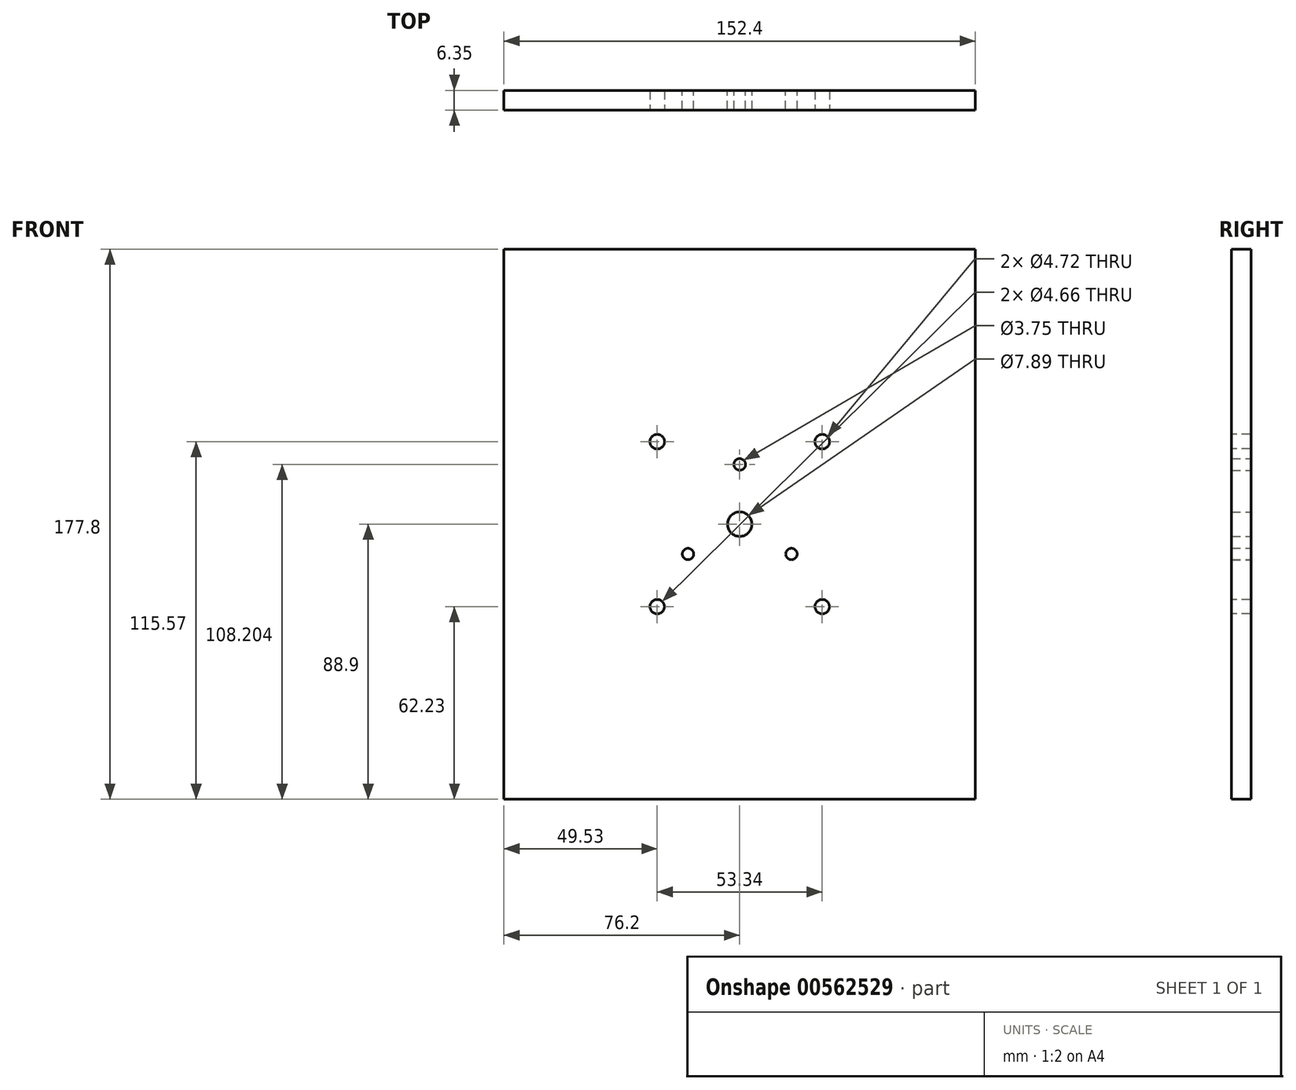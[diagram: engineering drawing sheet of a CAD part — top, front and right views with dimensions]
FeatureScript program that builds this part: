
annotation { "Feature Type Name" : "Feature", "Feature Type Description" : "" }
export const myFeature = defineFeature(function(context is Context, id is Id, definition is map)
    precondition{}
    {
        {
            var Q0;
            Q0=qCreatedBy(makeId("Front.planeOp"),FACE);
            var sketch = newSketch(context, id + "F0", { "sketchPlane" : qUnion([Q0])});
            skLineSegment(sketch, "E0.bottom", {"start": v(76.2, 88.9) * mm, "end": v(-76.2, 88.9) * mm});
            skLineSegment(sketch, "E0.top", {"start": v(76.2, -88.9) * mm, "end": v(-76.2, -88.9) * mm});
            skLineSegment(sketch, "E0.left", {"start": v(76.2, 88.9) * mm, "end": v(76.2, -88.9) * mm});
            skLineSegment(sketch, "E0.right", {"start": v(-76.2, 88.9) * mm, "end": v(-76.2, -88.9) * mm});
            skPoint(sketch, "E0.middle", {"position": v(0, 0) * mm});
            skLineSegment(sketch, "E1", {"start": v(0, 0) * mm, "end": v(0, 83.85) * mm, "construction": true});
            skLineSegment(sketch, "E2", {"start": v(0, 0) * mm, "end": v(67.53, -38.99) * mm, "construction": true});
            skLineSegment(sketch, "E3", {"start": v(0, 0) * mm, "end": v(-59.92, -34.6) * mm, "construction": true});
            skLineSegment(sketch, "E4", {"start": v(-11.78, 19.3) * mm, "end": v(15.02, 19.3) * mm, "construction": true});
            skLineSegment(sketch, "E5", {"start": v(20.55, -3.01) * mm, "end": v(11.36, -18.94) * mm, "construction": true});
            skLineSegment(sketch, "E6", {"start": v(-21.54, -0.84) * mm, "end": v(-10.74, -20.58) * mm, "construction": true});
            skCircle(sketch, "E7", {"center": v(-16.72, -9.65) * mm, "radius": 1.84 * mm});
            skCircle(sketch, "E8", {"center": v(16.72, -9.65) * mm, "radius": 1.85 * mm});
            skCircle(sketch, "E9", {"center": v(0, 19.3) * mm, "radius": 1.87 * mm});
            skCircle(sketch, "E10", {"center": v(0, 0) * mm, "radius": 3.94 * mm});
            skSolve(sketch);
        }
        {
            var Q0;
            Q0=makeQuery(id+"F0.imprint","IMPRINT",FACE,{"disambiguationData":[TD([[makeQuery(id+"F0.imprint","IMPRINT",EDGE,{"derivedFrom":sQuery(id+"F0.wireOp",EDGE,"E0.bottom")}),1.0]])]});
            extrude(context, id + "F1", {"entities" : qUnion([Q0]), "depth" : 6.35 * mm, "offsetDistance" : 25.4 * mm});
        }
        {
            var Q0;
            Q0=makeQuery(id+"F1.opExtrude","CAP_FACE",FACE,{"disambiguationData":[OSD([sQuery(id+"F0.wireOp",EDGE,"E0.bottom"),sQuery(id+"F0.wireOp",EDGE,"E0.top"),sQuery(id+"F0.wireOp",EDGE,"E0.left"),sQuery(id+"F0.wireOp",EDGE,"E0.right"),sQuery(id+"F0.wireOp",EDGE,"E7"),sQuery(id+"F0.wireOp",EDGE,"E8"),sQuery(id+"F0.wireOp",EDGE,"E9"),sQuery(id+"F0.wireOp",EDGE,"E10")])],"isStart":false});
            var sketch = newSketch(context, id + "F2", { "sketchPlane" : qUnion([Q0])});
            skCircle(sketch, "E11.cCircle", {"center": v(0, 0) * mm, "radius": 26.67 * mm, "construction": true});
            skPoint(sketch, "E11.0.midPoint", {"position": v(26.67, 0) * mm});
            skCircle(sketch, "E12", {"center": v(-26.67, 26.67) * mm, "radius": 2.36 * mm});
            skCircle(sketch, "E13", {"center": v(26.67, 26.67) * mm, "radius": 2.36 * mm});
            skCircle(sketch, "E14", {"center": v(26.67, -26.67) * mm, "radius": 2.33 * mm});
            skCircle(sketch, "E15", {"center": v(-26.67, -26.67) * mm, "radius": 2.33 * mm});
            skSolve(sketch);
        }
        {
            var Q0;
            Q0=makeQuery(id+"F2.imprint","IMPRINT",FACE,{"disambiguationData":[TD([[makeQuery(id+"F2.imprint","IMPRINT",EDGE,{"derivedFrom":sQuery(id+"F2.wireOp",EDGE,"E13")}),1.0]])]});
            var Q1;
            Q1=makeQuery(id+"F2.imprint","IMPRINT",FACE,{"disambiguationData":[TD([[makeQuery(id+"F2.imprint","IMPRINT",EDGE,{"derivedFrom":sQuery(id+"F2.wireOp",EDGE,"E14")}),1.0]])]});
            var Q2;
            Q2=makeQuery(id+"F2.imprint","IMPRINT",FACE,{"disambiguationData":[TD([[makeQuery(id+"F2.imprint","IMPRINT",EDGE,{"derivedFrom":sQuery(id+"F2.wireOp",EDGE,"E15")}),1.0]])]});
            var Q3;
            Q3=makeQuery(id+"F2.imprint","IMPRINT",FACE,{"disambiguationData":[TD([[makeQuery(id+"F2.imprint","IMPRINT",EDGE,{"derivedFrom":sQuery(id+"F2.wireOp",EDGE,"E12")}),1.0]])]});
            extrude(context, id + "F3", {"entities" : qUnion([Q0, Q1, Q2, Q3]), "operationType" : NewBodyOperationType.REMOVE, "endBound" : BoundingType.THROUGH_ALL, "oppositeDirection" : true, "depth" : 25.4 * mm, "offsetDistance" : 25.4 * mm});
        }
    });
